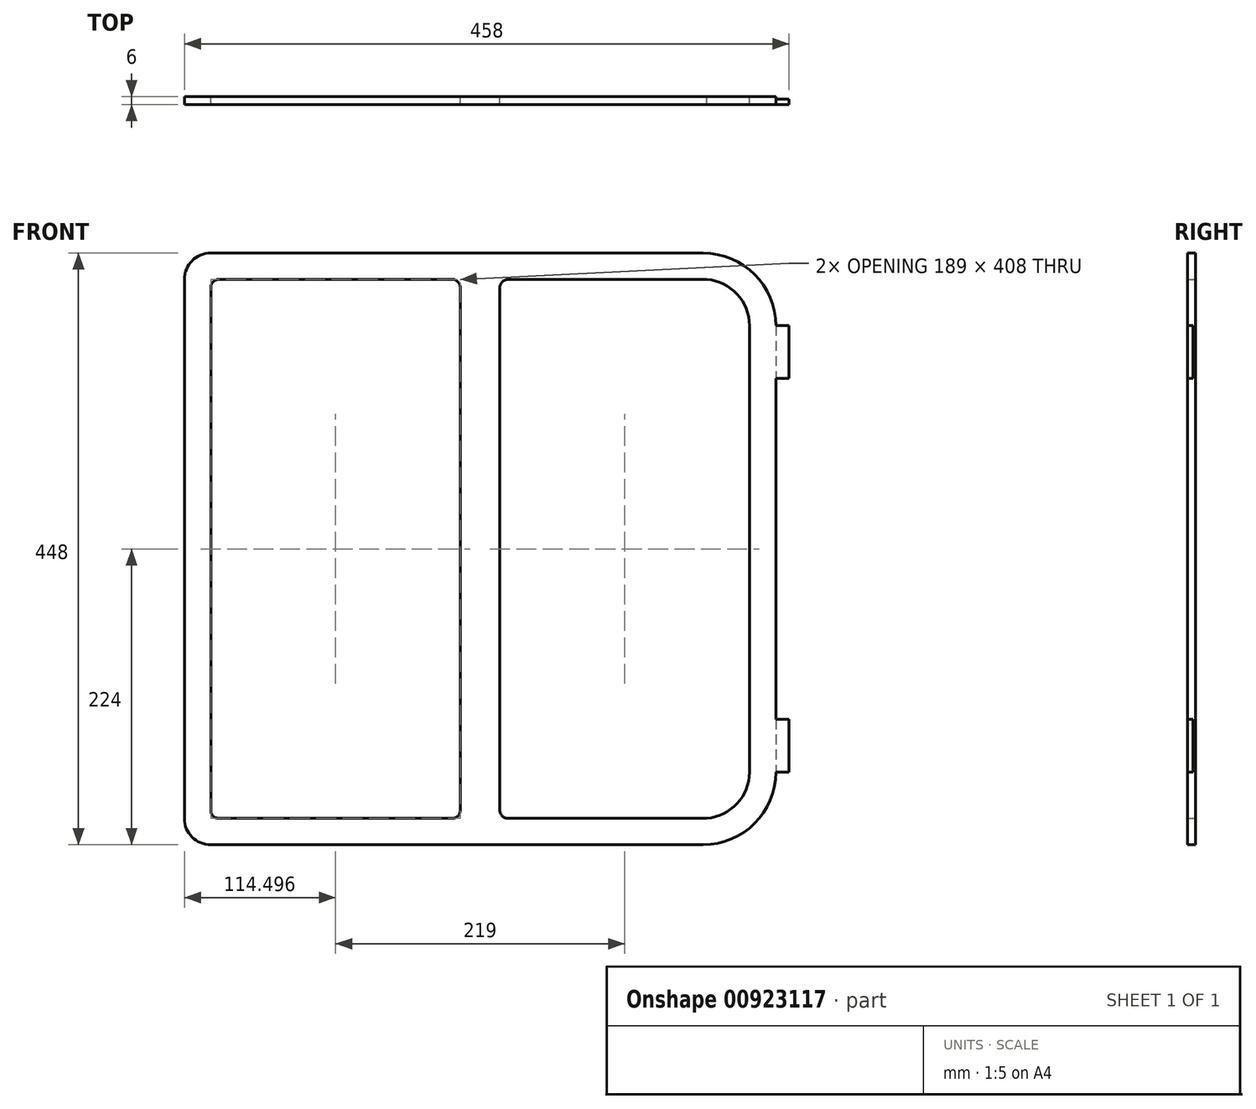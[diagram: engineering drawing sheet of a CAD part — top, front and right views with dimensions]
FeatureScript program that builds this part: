
annotation { "Feature Type Name" : "Feature", "Feature Type Description" : "" }
export const myFeature = defineFeature(function(context is Context, id is Id, definition is map)
    precondition{}
    {
        {
            var Q0;
            Q0=qCreatedBy(makeId("Front.planeOp"),FACE);
            var sketch = newSketch(context, id + "F0", { "sketchPlane" : qUnion([Q0])});
            skLineSegment(sketch, "E0.bottom", {"start": v(-187.42, 225.53) * mm, "end": v(185.58, 225.53) * mm});
            skLineSegment(sketch, "E0.top", {"start": v(-187.42, -222.47) * mm, "end": v(185.58, -222.47) * mm});
            skLineSegment(sketch, "E0.left", {"start": v(-207.42, 205.53) * mm, "end": v(-207.42, -202.47) * mm});
            skLineSegment(sketch, "E0.right", {"start": v(240.58, 170.53) * mm, "end": v(240.58, -167.47) * mm});
            skArc(sketch, "E1.filletArc", {"start": v(-187.42, 225.53) * mm, "mid": v(-201.57, 219.67) * mm, "end": v(-207.42, 205.53) * mm});
            skPoint(sketch, "E2.visualSharp", {"position": v(-207.42, -222.47) * mm});
            skArc(sketch, "E2.filletArc", {"start": v(-207.42, -202.47) * mm, "mid": v(-201.57, -216.61) * mm, "end": v(-187.42, -222.47) * mm});
            skPoint(sketch, "E3.visualSharp", {"position": v(240.58, 225.53) * mm});
            skArc(sketch, "E3.filletArc", {"start": v(240.58, 170.53) * mm, "mid": v(224.47, 209.42) * mm, "end": v(185.58, 225.53) * mm});
            skPoint(sketch, "E4.visualSharp", {"position": v(240.58, -222.47) * mm});
            skArc(sketch, "E4.filletArc", {"start": v(185.58, -222.47) * mm, "mid": v(224.47, -206.36) * mm, "end": v(240.58, -167.47) * mm});
            skArc(sketch, "E5.0", {"start": v(250.58, 170.53) * mm, "mid": v(231.54, 216.5) * mm, "end": v(185.58, 235.53) * mm});
            skArc(sketch, "E6.0", {"start": v(-217.42, -202.47) * mm, "mid": v(-208.64, -223.68) * mm, "end": v(-187.42, -232.47) * mm});
            skLineSegment(sketch, "E7.0", {"start": v(-217.42, 205.53) * mm, "end": v(-217.42, -202.47) * mm});
            skLineSegment(sketch, "E8.0", {"start": v(-187.42, -232.47) * mm, "end": v(185.58, -232.47) * mm});
            skArc(sketch, "E9.2", {"start": v(185.58, -232.47) * mm, "mid": v(231.54, -213.43) * mm, "end": v(250.58, -167.47) * mm});
            skLineSegment(sketch, "E9.4", {"start": v(250.58, 170.53) * mm, "end": v(250.58, -167.47) * mm});
            skLineSegment(sketch, "E9.6", {"start": v(-187.42, 235.53) * mm, "end": v(185.58, 235.53) * mm});
            skArc(sketch, "E9.7", {"start": v(-187.42, 235.53) * mm, "mid": v(-208.64, 226.74) * mm, "end": v(-217.42, 205.53) * mm});
            skArc(sketch, "E10.0", {"start": v(-201.42, -202.47) * mm, "mid": v(-197.32, -212.37) * mm, "end": v(-187.42, -216.47) * mm});
            skLineSegment(sketch, "E10.1", {"start": v(-201.42, 205.53) * mm, "end": v(-201.42, -202.47) * mm});
            skLineSegment(sketch, "E10.2", {"start": v(-187.42, -216.47) * mm, "end": v(185.58, -216.47) * mm});
            skArc(sketch, "E10.3", {"start": v(-187.42, 219.53) * mm, "mid": v(-197.32, 215.43) * mm, "end": v(-201.42, 205.53) * mm});
            skArc(sketch, "E10.4", {"start": v(185.58, -216.47) * mm, "mid": v(220.22, -202.12) * mm, "end": v(234.58, -167.47) * mm});
            skLineSegment(sketch, "E10.5", {"start": v(234.58, 170.53) * mm, "end": v(234.58, -167.47) * mm});
            skArc(sketch, "E10.6", {"start": v(234.58, 170.53) * mm, "mid": v(220.22, 205.18) * mm, "end": v(185.58, 219.53) * mm});
            skLineSegment(sketch, "E10.7", {"start": v(-187.42, 219.53) * mm, "end": v(185.58, 219.53) * mm});
            skLineSegment(sketch, "E11.0", {"start": v(-187.42, 199.53) * mm, "end": v(-187.42, -196.47) * mm});
            skLineSegment(sketch, "E11.1", {"start": v(-187.42, 205.53) * mm, "end": v(-187.42, 205.53) * mm});
            skLineSegment(sketch, "E11.3", {"start": v(-181.42, 205.53) * mm, "end": v(-4.42, 205.53) * mm});
            skLineSegment(sketch, "E11.4", {"start": v(-181.42, -202.47) * mm, "end": v(-4.42, -202.47) * mm});
            skArc(sketch, "E11.5", {"start": v(188.33, -202.47) * mm, "mid": v(211.32, -191.3) * mm, "end": v(220.58, -167.47) * mm});
            skLineSegment(sketch, "E11.6", {"start": v(220.58, 170.53) * mm, "end": v(220.58, -167.47) * mm});
            skArc(sketch, "E11.7", {"start": v(220.58, 170.53) * mm, "mid": v(211.32, 194.35) * mm, "end": v(188.33, 205.53) * mm});
            skArc(sketch, "E12.filletArc", {"start": v(-187.42, -196.47) * mm, "mid": v(-185.67, -200.71) * mm, "end": v(-181.42, -202.47) * mm});
            skArc(sketch, "E13.filletArc", {"start": v(-181.42, 205.53) * mm, "mid": v(-185.67, 203.77) * mm, "end": v(-187.42, 199.53) * mm});
            skLineSegment(sketch, "E14", {"start": v(220.58, 170.53) * mm, "end": v(250.58, 170.53) * mm});
            skLineSegment(sketch, "E15", {"start": v(220.58, -167.47) * mm, "end": v(250.58, -167.47) * mm});
            skLineSegment(sketch, "E16.0", {"start": v(220.58, 130.53) * mm, "end": v(250.58, 130.53) * mm});
            skLineSegment(sketch, "E17.0", {"start": v(220.58, -127.47) * mm, "end": v(250.58, -127.47) * mm});
            skLineSegment(sketch, "E18", {"start": v(31.58, 199.53) * mm, "end": v(31.58, -196.47) * mm});
            skLineSegment(sketch, "E19.0", {"start": v(1.58, 199.53) * mm, "end": v(1.58, -196.47) * mm});
            skArc(sketch, "E20.filletArc", {"start": v(1.58, 199.53) * mm, "mid": v(-0.18, 203.77) * mm, "end": v(-4.42, 205.53) * mm});
            skArc(sketch, "E21.filletArc", {"start": v(-4.42, -202.47) * mm, "mid": v(-0.18, -200.71) * mm, "end": v(1.58, -196.47) * mm});
            skLineSegment(sketch, "E22", {"start": v(37.58, 205.53) * mm, "end": v(188.33, 205.53) * mm});
            skLineSegment(sketch, "E23", {"start": v(37.58, -202.47) * mm, "end": v(188.33, -202.47) * mm});
            skPoint(sketch, "E24.visualSharp", {"position": v(31.58, 205.53) * mm});
            skArc(sketch, "E24.filletArc", {"start": v(37.58, 205.53) * mm, "mid": v(33.33, 203.77) * mm, "end": v(31.58, 199.53) * mm});
            skPoint(sketch, "E25.visualSharp", {"position": v(31.58, -202.47) * mm});
            skArc(sketch, "E25.filletArc", {"start": v(31.58, -196.47) * mm, "mid": v(33.33, -200.71) * mm, "end": v(37.58, -202.47) * mm});
            skSolve(sketch);
        }
        {
            var Q0;
            Q0=makeQuery(id+"F0.imprint","IMPRINT",FACE,{"disambiguationData":[TD([[makeQuery(id+"F0.imprint","IMPRINT",EDGE,{"derivedFrom":sQuery(id+"F0.wireOp",EDGE,"E0.bottom")}),-1.0]])]});
            var Q1;
            Q1=makeQuery(id+"F0.imprint","IMPRINT",FACE,{"disambiguationData":[TD([[makeQuery(id+"F0.imprint","IMPRINT",EDGE,{"derivedFrom":sQuery(id+"F0.wireOp",EDGE,"E10.0")}),1.0]])]});
            var Q2;
            {var subQ3=sQuery(id+"F0.wireOp",EDGE,"E16.0");var subQ5=sQuery(id+"F0.wireOp",EDGE,"E9.4");var subQ6=makeQuery(id+"F0.imprint","INTERSECT",VERTEX,{"derivedFrom":[subQ5,subQ3]});Q2=makeQuery(id+"F0.imprint","IMPRINT",FACE,{"disambiguationData":[TD([[makeQuery(id+"F0.imprint","IMPRINT",EDGE,{"disambiguationData":[TD([[subQ6,1.0]])],"derivedFrom":subQ3}),1.0]])]});}
            var Q3;
            {var subQ1=sQuery(id+"F0.wireOp",EDGE,"E0.right");var subQ3=sQuery(id+"F0.wireOp",EDGE,"E16.0");var subQ4=makeQuery(id+"F0.imprint","INTERSECT",VERTEX,{"derivedFrom":[subQ1,subQ3]});Q3=makeQuery(id+"F0.imprint","IMPRINT",FACE,{"disambiguationData":[TD([[makeQuery(id+"F0.imprint","IMPRINT",EDGE,{"disambiguationData":[TD([[subQ4,1.0]])],"derivedFrom":subQ3}),1.0]])]});}
            var Q4;
            {var subQ3=sQuery(id+"F0.wireOp",EDGE,"E16.0");var subQ5=sQuery(id+"F0.wireOp",EDGE,"E11.6");var subQ7=makeQuery(id+"F0.imprint","INTERSECT",VERTEX,{"derivedFrom":[subQ5,subQ3]});Q4=makeQuery(id+"F0.imprint","IMPRINT",FACE,{"disambiguationData":[TD([[makeQuery(id+"F0.imprint","IMPRINT",EDGE,{"disambiguationData":[TD([[subQ7,-1.0]])],"derivedFrom":subQ3}),1.0]])]});}
            var Q5;
            {var subQ0=sQuery(id+"F0.wireOp",EDGE,"E16.0");var subQ1=sQuery(id+"F0.wireOp",EDGE,"E10.5");var subQ2=makeQuery(id+"F0.imprint","INTERSECT",VERTEX,{"derivedFrom":[subQ1,subQ0]});Q5=makeQuery(id+"F0.imprint","IMPRINT",FACE,{"disambiguationData":[TD([[makeQuery(id+"F0.imprint","IMPRINT",EDGE,{"disambiguationData":[TD([[subQ2,-1.0]])],"derivedFrom":subQ1}),-1.0]])]});}
            var Q6;
            {var subQ0=sQuery(id+"F0.wireOp",EDGE,"E16.0");var subQ1=sQuery(id+"F0.wireOp",EDGE,"E0.right");var subQ2=makeQuery(id+"F0.imprint","INTERSECT",VERTEX,{"derivedFrom":[subQ1,subQ0]});Q6=makeQuery(id+"F0.imprint","IMPRINT",FACE,{"disambiguationData":[TD([[makeQuery(id+"F0.imprint","IMPRINT",EDGE,{"disambiguationData":[TD([[subQ2,-1.0]])],"derivedFrom":subQ1}),-1.0]])]});}
            var Q7;
            {var subQ1=sQuery(id+"F0.wireOp",EDGE,"E0.right");var subQ3=sQuery(id+"F0.wireOp",EDGE,"E17.0");var subQ4=makeQuery(id+"F0.imprint","INTERSECT",VERTEX,{"derivedFrom":[subQ1,subQ3]});Q7=makeQuery(id+"F0.imprint","IMPRINT",FACE,{"disambiguationData":[TD([[makeQuery(id+"F0.imprint","IMPRINT",EDGE,{"disambiguationData":[TD([[subQ4,1.0]])],"derivedFrom":subQ3}),-1.0]])]});}
            var Q8;
            {var subQ3=sQuery(id+"F0.wireOp",EDGE,"E17.0");var subQ5=sQuery(id+"F0.wireOp",EDGE,"E11.6");var subQ7=makeQuery(id+"F0.imprint","INTERSECT",VERTEX,{"derivedFrom":[subQ5,subQ3]});Q8=makeQuery(id+"F0.imprint","IMPRINT",FACE,{"disambiguationData":[TD([[makeQuery(id+"F0.imprint","IMPRINT",EDGE,{"disambiguationData":[TD([[subQ7,-1.0]])],"derivedFrom":subQ3}),-1.0]])]});}
            var Q9;
            {var subQ3=sQuery(id+"F0.wireOp",EDGE,"E17.0");var subQ5=sQuery(id+"F0.wireOp",EDGE,"E9.4");var subQ7=makeQuery(id+"F0.imprint","INTERSECT",VERTEX,{"derivedFrom":[subQ5,subQ3]});Q9=makeQuery(id+"F0.imprint","IMPRINT",FACE,{"disambiguationData":[TD([[makeQuery(id+"F0.imprint","IMPRINT",EDGE,{"disambiguationData":[TD([[subQ7,1.0]])],"derivedFrom":subQ3}),-1.0]])]});}
            extrude(context, id + "F1", {"entities" : qUnion([Q0, Q1, Q2, Q3, Q4, Q5, Q6, Q7, Q8, Q9]), "depth" : 6 * mm, "offsetDistance" : 25 * mm});
        }
        {
            var Q0;
            {var subQ3=sQuery(id+"F0.wireOp",EDGE,"E16.0");var subQ5=sQuery(id+"F0.wireOp",EDGE,"E9.4");var subQ6=makeQuery(id+"F0.imprint","INTERSECT",VERTEX,{"derivedFrom":[subQ5,subQ3]});Q0=makeQuery(id+"F0.imprint","IMPRINT",FACE,{"disambiguationData":[TD([[makeQuery(id+"F0.imprint","IMPRINT",EDGE,{"disambiguationData":[TD([[subQ6,1.0]])],"derivedFrom":subQ3}),1.0]])]});}
            var Q1;
            {var subQ3=sQuery(id+"F0.wireOp",EDGE,"E17.0");var subQ5=sQuery(id+"F0.wireOp",EDGE,"E9.4");var subQ7=makeQuery(id+"F0.imprint","INTERSECT",VERTEX,{"derivedFrom":[subQ5,subQ3]});Q1=makeQuery(id+"F0.imprint","IMPRINT",FACE,{"disambiguationData":[TD([[makeQuery(id+"F0.imprint","IMPRINT",EDGE,{"disambiguationData":[TD([[subQ7,1.0]])],"derivedFrom":subQ3}),-1.0]])]});}
            extrude(context, id + "F2", {"entities" : qUnion([Q0, Q1]), "operationType" : NewBodyOperationType.REMOVE, "depth" : 2 * mm, "offsetDistance" : 25 * mm});
        }
    });
